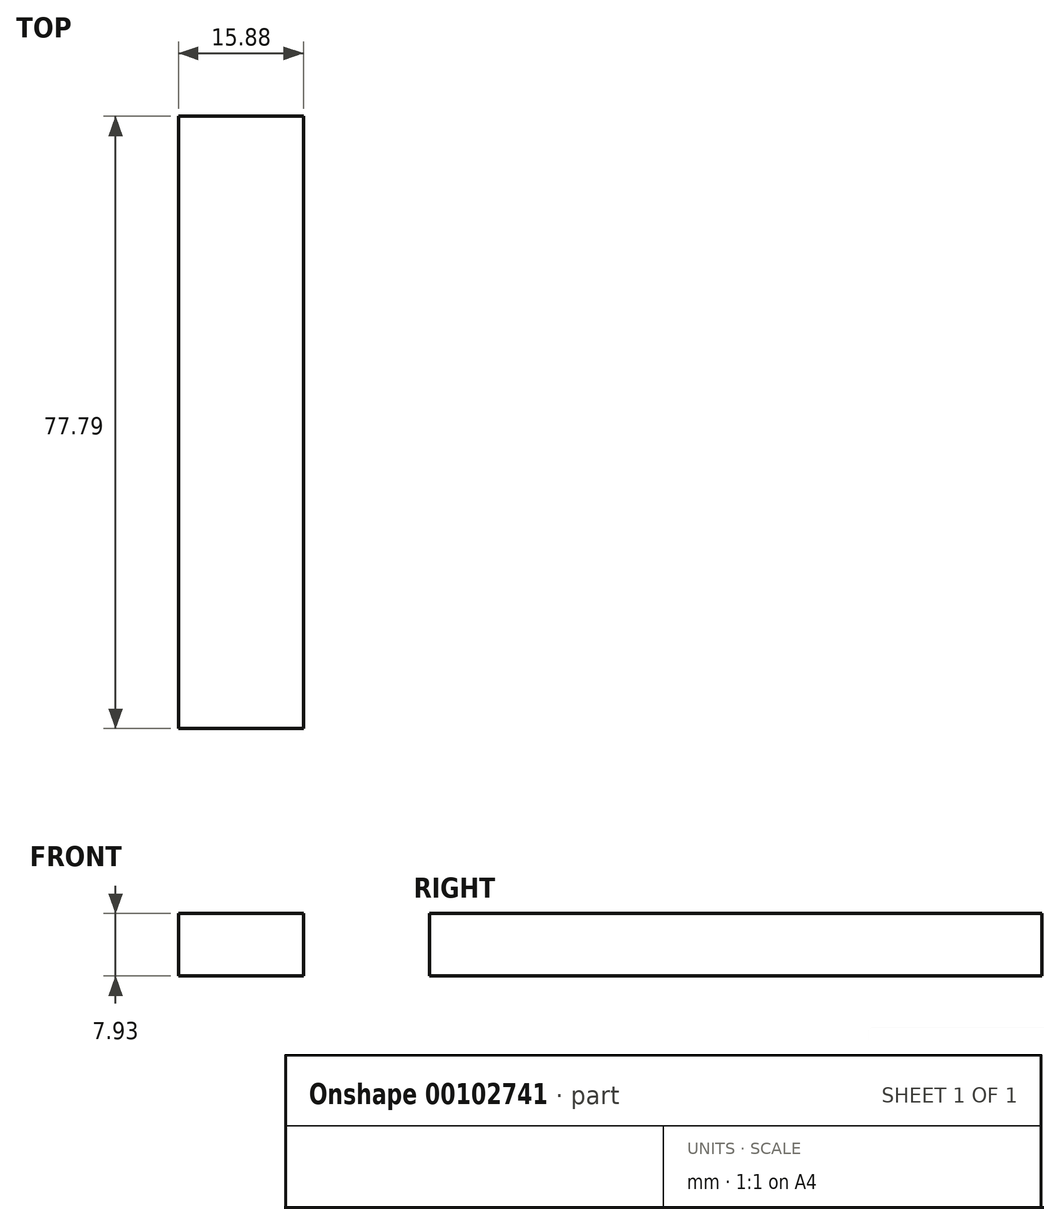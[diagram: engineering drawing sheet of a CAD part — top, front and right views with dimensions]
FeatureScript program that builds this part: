
annotation { "Feature Type Name" : "Feature", "Feature Type Description" : "" }
export const myFeature = defineFeature(function(context is Context, id is Id, definition is map)
    precondition{}
    {
        {
            var Q0;
            Q0=qCreatedBy(makeId("Front.planeOp"),FACE);
            var sketch = newSketch(context, id + "F0", { "sketchPlane" : qUnion([Q0])});
            skLineSegment(sketch, "E0.bottom", {"start": v(-6.73, 7.14) * mm, "end": v(9.15, 7.14) * mm});
            skLineSegment(sketch, "E0.top", {"start": v(-6.73, -0.8) * mm, "end": v(9.15, -0.8) * mm});
            skLineSegment(sketch, "E0.left", {"start": v(-6.73, 7.14) * mm, "end": v(-6.73, -0.8) * mm});
            skLineSegment(sketch, "E0.right", {"start": v(9.15, 7.14) * mm, "end": v(9.15, -0.8) * mm});
            skSolve(sketch);
        }
        {
            var Q0;
            Q0=makeQuery(id+"F0.imprint","IMPRINT",FACE,{"disambiguationData":[TD([[makeQuery(id+"F0.imprint","IMPRINT",EDGE,{"derivedFrom":sQuery(id+"F0.wireOp",EDGE,"E0.bottom")}),-1.0]])]});
            extrude(context, id + "F1", {"entities" : qUnion([Q0]), "depth" : 77.8 * mm});
        }
    });
